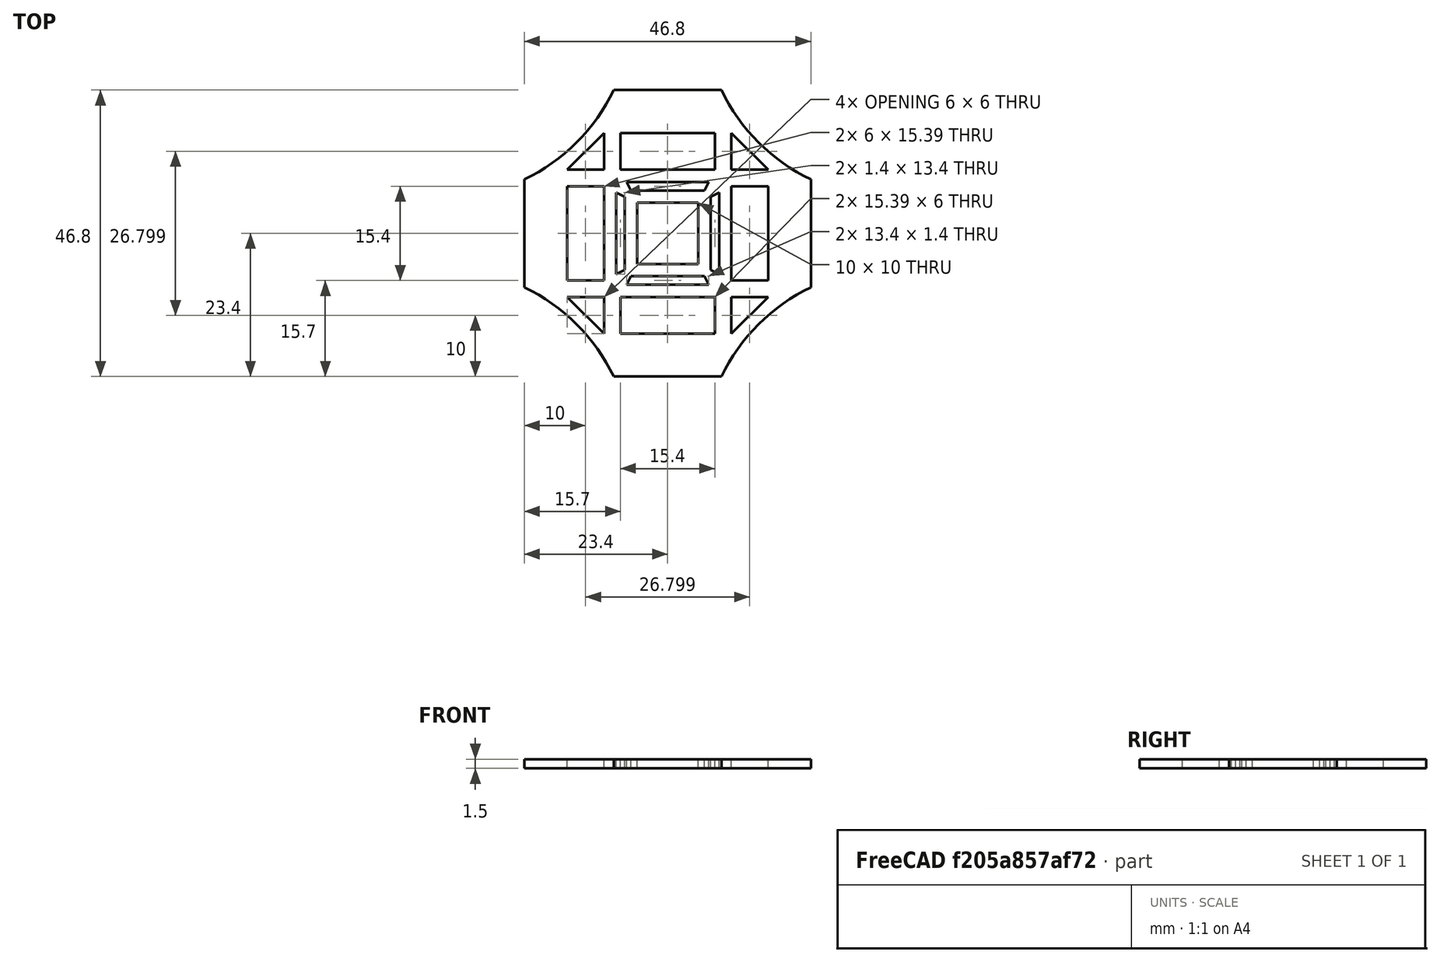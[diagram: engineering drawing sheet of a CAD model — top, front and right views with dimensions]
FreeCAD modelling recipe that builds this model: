
FCSTD DOCUMENT  (FreeCAD 0.19R23578 (Git))
Label: base
License: All rights reserved
LicenseURL: http://en.wikipedia.org/wiki/All_rights_reserved
objects: Part::Feature×14, Part::Extrusion×14, Part::Cut×13
note: 41 computed .brp shape members not serialized (recipe doc carries the construction recipe); baked Part::Feature solids carry a one-line shape summary decoded from their .brp

FEATURE [Part::Feature] Face
  shape: bbox 6 x 6 x 2e-07 mm, 1 faces, 0 solids (baked)
FEATURE [Part::Feature] Face001
  shape: bbox 15.39 x 6 x 2e-07 mm, 1 faces, 0 solids (baked)
FEATURE [Part::Feature] Face002
  shape: bbox 6 x 6 x 2e-07 mm, 1 faces, 0 solids (baked)
FEATURE [Part::Feature] Face003
  shape: bbox 6 x 15.39 x 2e-07 mm, 1 faces, 0 solids (baked)
FEATURE [Part::Feature] Face004
  shape: bbox 6 x 6 x 2e-07 mm, 1 faces, 0 solids (baked)
FEATURE [Part::Feature] Face005
  shape: bbox 1.4 x 13.4 x 2e-07 mm, 1 faces, 0 solids (baked)
FEATURE [Part::Feature] Face006
  shape: bbox 13.4 x 1.4 x 2e-07 mm, 1 faces, 0 solids (baked)
FEATURE [Part::Feature] Face007
  shape: bbox 10 x 10 x 2e-07 mm, 1 faces, 0 solids (baked)
FEATURE [Part::Feature] Face008
  shape: bbox 13.4 x 1.4 x 2e-07 mm, 1 faces, 0 solids (baked)
FEATURE [Part::Feature] Face009
  shape: bbox 1.4 x 13.4 x 2e-07 mm, 1 faces, 0 solids (baked)
FEATURE [Part::Feature] Face010
  shape: bbox 6 x 15.39 x 2e-07 mm, 1 faces, 0 solids (baked)
FEATURE [Part::Feature] Face011
  shape: bbox 6 x 6 x 2e-07 mm, 1 faces, 0 solids (baked)
FEATURE [Part::Feature] Face012
  shape: bbox 15.39 x 6 x 2e-07 mm, 1 faces, 0 solids (baked)
FEATURE [Part::Feature] Face013
  shape: bbox 46.8 x 46.8 x 2e-07 mm, 1 faces, 0 solids (baked)
FEATURE [Part::Extrusion] Extrude
  Base = -> Face013
  Dir = (0,0,1)
  DirMode = 0
  FaceMakerClass = Part::FaceMakerBullseye
  LengthFwd = 1.5
  LengthRev = 0
  Solid = false
  Symmetric = false
FEATURE [Part::Extrusion] Extrude001
  Base = -> Face
  Dir = (0,0,1)
  DirMode = 0
  FaceMakerClass = Part::FaceMakerBullseye
  LengthFwd = 3
  LengthRev = 0
  Solid = false
  Symmetric = false
FEATURE [Part::Extrusion] Extrude002
  Base = -> Face001
  Dir = (0,0,1)
  DirMode = 0
  FaceMakerClass = Part::FaceMakerBullseye
  LengthFwd = 3
  LengthRev = 0
  Solid = false
  Symmetric = false
FEATURE [Part::Extrusion] Extrude003
  Base = -> Face002
  Dir = (0,0,1)
  DirMode = 0
  FaceMakerClass = Part::FaceMakerBullseye
  LengthFwd = 3
  LengthRev = 0
  Solid = false
  Symmetric = false
FEATURE [Part::Extrusion] Extrude004
  Base = -> Face003
  Dir = (0,0,1)
  DirMode = 0
  FaceMakerClass = Part::FaceMakerBullseye
  LengthFwd = 3
  LengthRev = 0
  Solid = false
  Symmetric = false
FEATURE [Part::Extrusion] Extrude005
  Base = -> Face004
  Dir = (0,0,1)
  DirMode = 0
  FaceMakerClass = Part::FaceMakerBullseye
  LengthFwd = 3
  LengthRev = 0
  Solid = false
  Symmetric = false
FEATURE [Part::Extrusion] Extrude006
  Base = -> Face005
  Dir = (0,0,1)
  DirMode = 0
  FaceMakerClass = Part::FaceMakerBullseye
  LengthFwd = 3
  LengthRev = 0
  Solid = false
  Symmetric = false
FEATURE [Part::Extrusion] Extrude007
  Base = -> Face006
  Dir = (0,0,1)
  DirMode = 0
  FaceMakerClass = Part::FaceMakerBullseye
  LengthFwd = 3
  LengthRev = 0
  Solid = false
  Symmetric = false
FEATURE [Part::Extrusion] Extrude008
  Base = -> Face007
  Dir = (0,0,1)
  DirMode = 0
  FaceMakerClass = Part::FaceMakerBullseye
  LengthFwd = 3
  LengthRev = 0
  Solid = false
  Symmetric = false
FEATURE [Part::Extrusion] Extrude009
  Base = -> Face008
  Dir = (0,0,1)
  DirMode = 0
  FaceMakerClass = Part::FaceMakerBullseye
  LengthFwd = 3
  LengthRev = 0
  Solid = false
  Symmetric = false
FEATURE [Part::Extrusion] Extrude010
  Base = -> Face009
  Dir = (0,0,1)
  DirMode = 0
  FaceMakerClass = Part::FaceMakerBullseye
  LengthFwd = 3
  LengthRev = 0
  Solid = false
  Symmetric = false
FEATURE [Part::Extrusion] Extrude011
  Base = -> Face010
  Dir = (0,0,1)
  DirMode = 0
  FaceMakerClass = Part::FaceMakerBullseye
  LengthFwd = 3
  LengthRev = 0
  Solid = false
  Symmetric = false
FEATURE [Part::Extrusion] Extrude012
  Base = -> Face011
  Dir = (0,0,1)
  DirMode = 0
  FaceMakerClass = Part::FaceMakerBullseye
  LengthFwd = 3
  LengthRev = 0
  Solid = false
  Symmetric = false
FEATURE [Part::Extrusion] Extrude013
  Base = -> Face012
  Dir = (0,0,1)
  DirMode = 0
  FaceMakerClass = Part::FaceMakerBullseye
  LengthFwd = 3
  LengthRev = 0
  Solid = false
  Symmetric = false
FEATURE [Part::Cut] Cut
  Base = -> Extrude
  Tool = -> Extrude011
FEATURE [Part::Cut] Cut001
  Base = -> Cut
  Tool = -> Extrude013
FEATURE [Part::Cut] Cut002
  Base = -> Cut001
  Tool = -> Extrude012
FEATURE [Part::Cut] Cut003
  Base = -> Cut002
  Tool = -> Extrude010
FEATURE [Part::Cut] Cut004
  Base = -> Cut003
  Tool = -> Extrude009
FEATURE [Part::Cut] Cut005
  Base = -> Cut004
  Tool = -> Extrude008
FEATURE [Part::Cut] Cut006
  Base = -> Cut005
  Tool = -> Extrude007
FEATURE [Part::Cut] Cut007
  Base = -> Cut006
  Tool = -> Extrude006
FEATURE [Part::Cut] Cut008
  Base = -> Cut007
  Tool = -> Extrude005
FEATURE [Part::Cut] Cut009
  Base = -> Cut008
  Tool = -> Extrude004
FEATURE [Part::Cut] Cut010
  Base = -> Cut009
  Tool = -> Extrude003
FEATURE [Part::Cut] Cut011
  Base = -> Cut010
  Tool = -> Extrude002
FEATURE [Part::Cut] Cut012
  Base = -> Cut011
  Tool = -> Extrude001
